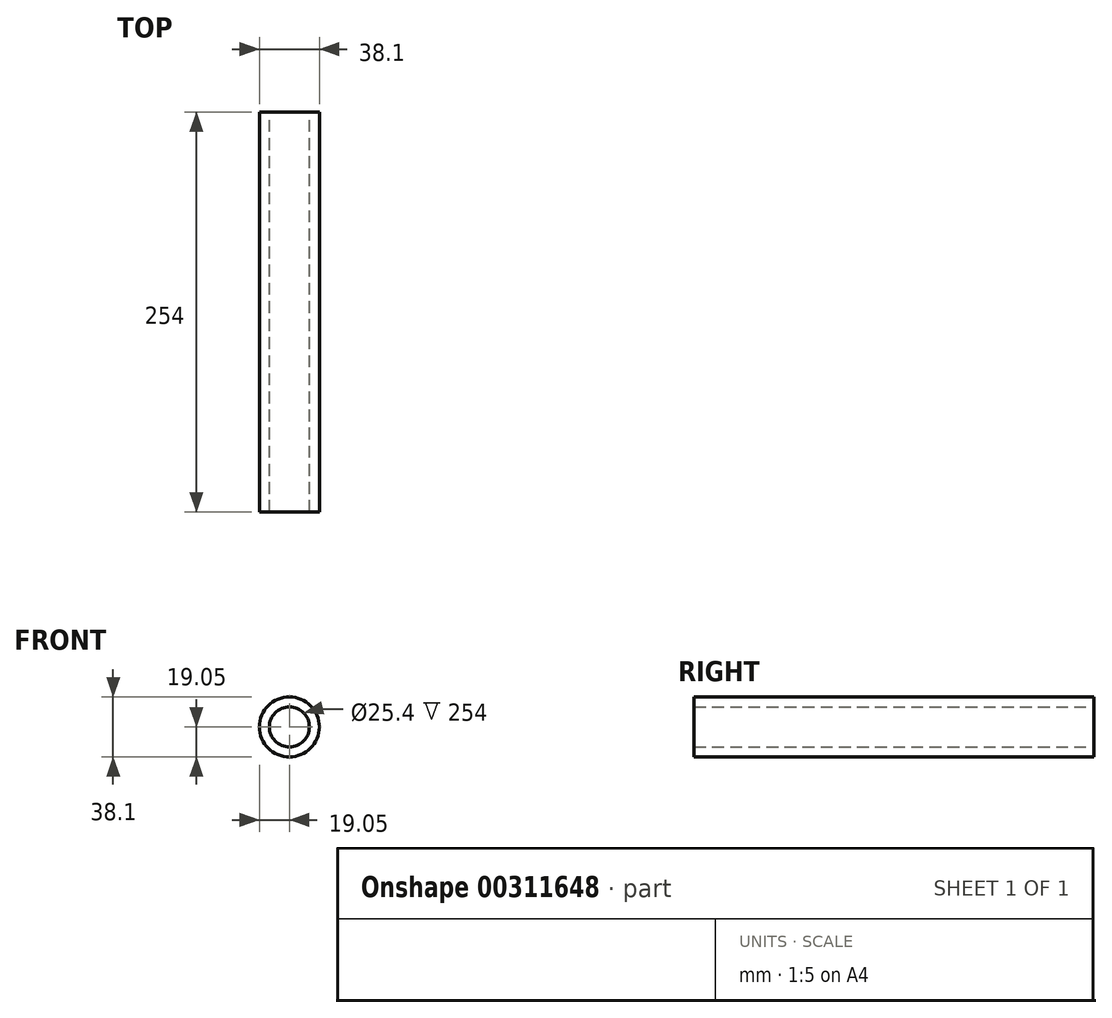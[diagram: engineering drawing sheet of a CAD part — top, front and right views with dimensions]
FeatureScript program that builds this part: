
annotation { "Feature Type Name" : "Feature", "Feature Type Description" : "" }
export const myFeature = defineFeature(function(context is Context, id is Id, definition is map)
    precondition{}
    {
        {
            var Q0;
            Q0=qCreatedBy(makeId("Front.planeOp"),FACE);
            var sketch = newSketch(context, id + "F0", { "sketchPlane" : qUnion([Q0])});
            skCircle(sketch, "E0", {"center": v(0, 0) * mm, "radius": 19.05 * mm});
            skCircle(sketch, "E1", {"center": v(0, 0) * mm, "radius": 12.7 * mm});
            skSolve(sketch);
        }
        {
            var Q0;
            Q0 = qSketchRegion(id + "F0", true);
            extrude(context, id + "F1", {"entities" : qUnion([Q0]), "depth" : 254 * mm});
        }
    });
